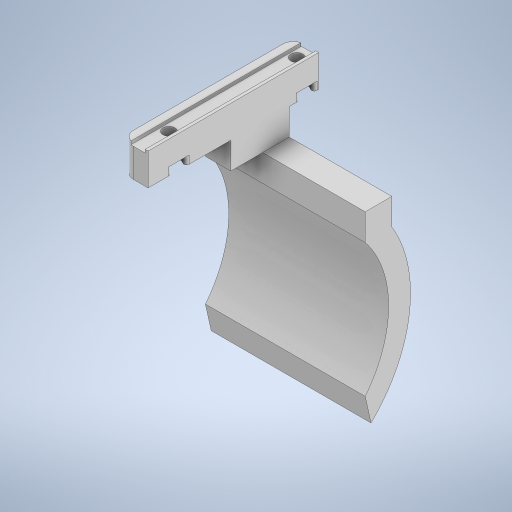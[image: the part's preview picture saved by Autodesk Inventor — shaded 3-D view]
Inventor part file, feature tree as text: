
AUTODESK INVENTOR PART (.ipt)
format: ipt  version: 2024 (Build 280153000, 153)  size: 339,456 bytes
history: native  units: in
note: dims shown in document units (in); Inventor stores cm internally (conversion verified against a paired STEP export)
features: sketch x7, extrude x5, projected_geometry x4, fillet x2, sweep x1
ambient origin geometry x8: Origin, YZ Plane, XZ Plane, XY Plane, X Axis, Y Axis, Z Axis, Center Point
bodies: Solid1 (feature_tree)
feature tree (19):
  extrude  "Extrusion1"  Depth=2.5197in
  extrude  "Extrusion2"  Depth=1.8898in
  extrude  "Extrusion3"  Depth=0.4724in TaperAngle=0.0deg
  fillet  "Fillet1"  Radius=0.0433in
  fillet  "Fillet2"  Radius=0.2126in
  extrude  "Extrusion19"  Depth=0.4724in TaperAngle=0.0deg
  extrude  "Extrusion20"  Depth=0.1181in TaperAngle=0.0deg
  sweep  "Sweep1"
  sketch  "Sketch1"  dims[d1=0.374in d2=2.5197in]
  sketch  "Sketch2"  dims[d3=0.1772in d4=1.8898in]
  sketch  "Sketch3"  dims[d6=0.1457in d7=0.4724in d8=0.0in d9=0.0433in d10=0.2126in]
  projected_geometry  "Projected Loop2"
  projected_geometry  "Projected Loop3"
  projected_geometry  "Projected Loop4"
  projected_geometry  "Projected Loop5"
  sketch  "Sketch28"  dims[d11=0.0472in d12=0.4724in d13=0.0in]
  sketch  "Sketch29"  dims[d14=0.2953in d15=0.1181in d16=0.0in]
  sketch  "Sketch30"  dims[d17=0.1772in d18=0.0394in]
  sketch  "Sketch31"  dims[d19=0.1575in d76=0.4724in d107=0.102in d108=0.8661in d109=0.3937in d110=0.0in d111=1.8898in d112=0.3937in d113=2.3622in d114=0.3937in d115=0.3937in d116=0.0in d117=1.9685in d118=1.5748in d119=0.0in d120=0.0in d42=0.0197in d43=0.0344in d44=0.0197in d45=0.0344in d46=0.0in d47=0.0in d48=0.0in d49=0.0in d50=0.0in d51=0.0in d52=0.0in d53=0.0in d55=0.0197in d56=0.0344in d57=0.0197in d58=0.0344in d60=0.0197in d61=0.0344in d62=0.0197in d63=0.0344in d72=0.0197in d73=0.0344in d74=0.0197in d75=0.0344in]
